# Revit family: Towel Rail-Single-Caroma Track
name_source: partatom
category: Specialty Equipment
revit_build: Autodesk Revit 2014 (Build: 20131024_2115(x64)
units: mm (PartAtom-declared; Revit-internal decimal feet)

## types (2) — shared parameters
Assembly Code = C1030200
Default Elevation = 900 mm  [stored 2.95276 ft]
Description = Featuring bold, designer styling and European inspired design, the Track range will lift the feel of any bathroom.
Height_ANZRS = 38 mm  [stored 0.124672 ft]
Manufacturer = GWA Bathrooms & Kitchens
Material_ANZRS = Metal-Chrome-Caroma
ModifiedIssue_ANZRS = 20150112 $
URL = http://specify.caroma.com.au
Width_ANZRS = 75 mm
zero-valued in all types: Cost

## per-type parameters (varying)
| type | Large | Length_ANZRS | Model | Type Comments |
| 800mm | Yes | 800 mm  [stored 2.62467 ft] | 90231C | Caroma Track Single Towel Rail - 800mm |
| 600mm | No | 600 mm | 90225C | Caroma Track Single Towel Rail - 600mm |

note: [stored X ft] marks values corroborated as IEEE doubles in the binary element streams (Revit-internal decimal feet)

## geometry (parser evidence)
native form markers: Blend x10, Sweep x1
no freeform markers — native parametric forms only
